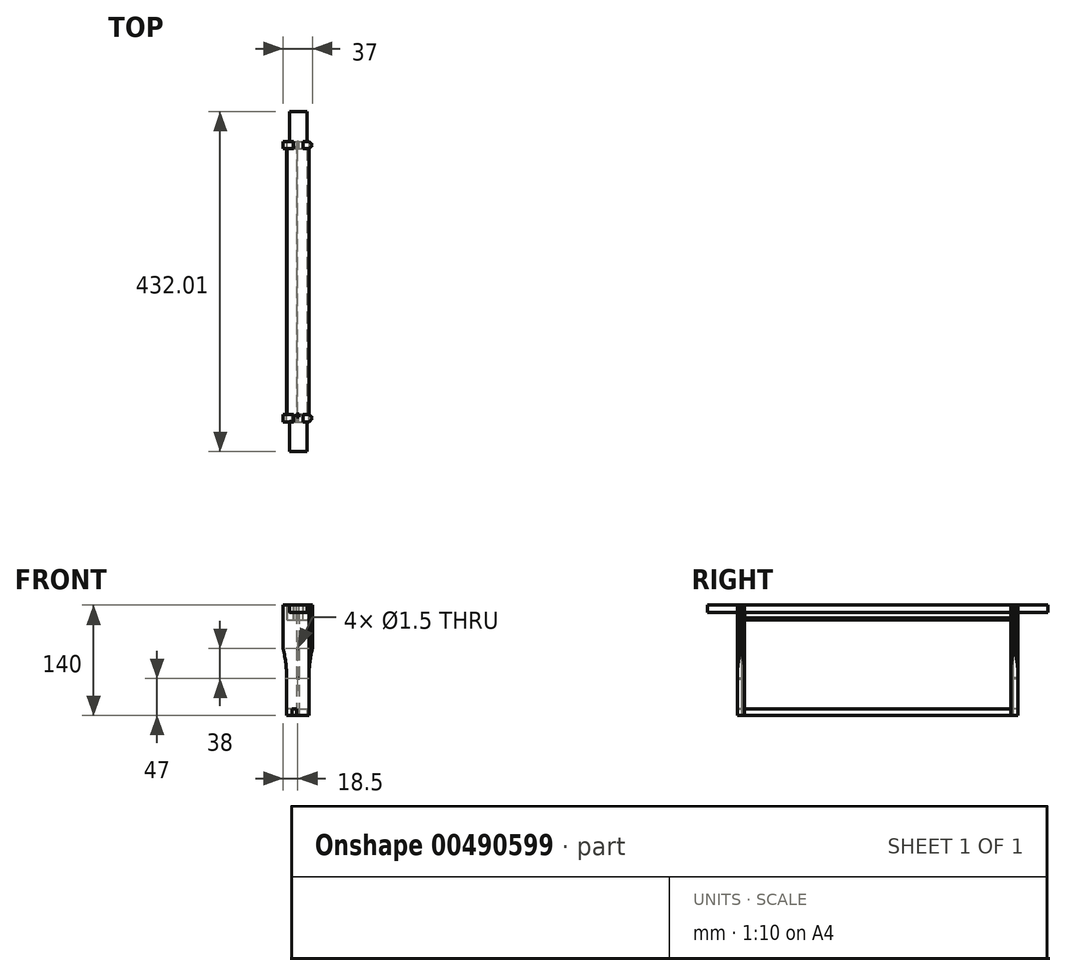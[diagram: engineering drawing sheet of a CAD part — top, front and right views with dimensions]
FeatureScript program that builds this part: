
annotation { "Feature Type Name" : "Feature", "Feature Type Description" : "" }
export const myFeature = defineFeature(function(context is Context, id is Id, definition is map)
    precondition{}
    {
        {
            var Q0;
            Q0=qCreatedBy(makeId("Top.planeOp"),FACE);
            var sketch = newSketch(context, id + "F0", { "sketchPlane" : qUnion([Q0])});
            skLineSegment(sketch, "E0", {"start": v(19.05, -9) * mm, "end": v(19.05, 383.16) * mm, "construction": true});
            skLineSegment(sketch, "E1.0", {"start": v(33.05, 0.03) * mm, "end": v(33.05, 338.03) * mm});
            skLineSegment(sketch, "E2.0", {"start": v(5.05, 0.04) * mm, "end": v(5.05, 338.03) * mm});
            skLineSegment(sketch, "E3.0", {"start": v(5.05, 338.03) * mm, "end": v(13.05, 338.03) * mm});
            skPoint(sketch, "E4.orphan", {"position": v(0.35, 338.03) * mm});
            skLineSegment(sketch, "E5.0", {"start": v(25.05, 338.04) * mm, "end": v(33.05, 338.03) * mm});
            skLineSegment(sketch, "E5.1", {"start": v(25.05, 347.04) * mm, "end": v(25.05, 338.04) * mm});
            skLineSegment(sketch, "E5.2", {"start": v(13.05, 347.03) * mm, "end": v(13.05, 338.03) * mm});
            skLineSegment(sketch, "E5.3", {"start": v(8.05, 347.03) * mm, "end": v(13.05, 347.03) * mm});
            skLineSegment(sketch, "E5.4", {"start": v(25.05, 347.04) * mm, "end": v(30.05, 347.04) * mm});
            skPoint(sketch, "E6.orphan", {"position": v(33.25, 338.03) * mm});
            skPoint(sketch, "E7.orphan", {"position": v(33.23, 347.04) * mm});
            skLineSegment(sketch, "E8", {"start": v(8.05, 347.03) * mm, "end": v(8.05, 385.04) * mm});
            skLineSegment(sketch, "E9", {"start": v(30.05, 347.04) * mm, "end": v(30.05, 385.04) * mm});
            skLineSegment(sketch, "E10", {"start": v(8.05, 385.04) * mm, "end": v(30.05, 385.04) * mm});
            skPoint(sketch, "E11.orphan", {"position": v(0.35, 347.03) * mm});
            skPoint(sketch, "E12.endSnap0", {"position": v(19.05, 187.08) * mm});
            skLineSegment(sketch, "E13.0", {"start": v(25.05, 0.03) * mm, "end": v(33.05, 0.03) * mm});
            skLineSegment(sketch, "E13.1", {"start": v(5.05, 0.04) * mm, "end": v(13.05, 0.04) * mm});
            skPoint(sketch, "E14.orphan", {"position": v(0, 0.04) * mm});
            skPoint(sketch, "E15.orphan", {"position": v(33.6, 0.03) * mm});
            skLineSegment(sketch, "E16", {"start": v(19.05, 169.03) * mm, "end": v(85.88, 169.03) * mm, "construction": true});
            skPoint(sketch, "E16.startSnap0", {"position": v(5.05, 169.03) * mm});
            skPoint(sketch, "E16.endSnap0", {"position": v(33.05, 169.03) * mm});
            skLineSegment(sketch, "E17.MirrorCS", {"start": v(8.05, -8.87) * mm, "end": v(13.05, -8.87) * mm});
            skLineSegment(sketch, "E18.MirrorCS", {"start": v(8.05, -8.87) * mm, "end": v(8.05, -46.97) * mm});
            skLineSegment(sketch, "E19.MirrorCS", {"start": v(8.05, -46.97) * mm, "end": v(30.05, -46.97) * mm});
            skLineSegment(sketch, "E20.MirrorCS", {"start": v(30.05, -8.97) * mm, "end": v(30.05, -46.97) * mm});
            skLineSegment(sketch, "E21.MirrorCS", {"start": v(25.05, -8.97) * mm, "end": v(30.05, -8.97) * mm});
            skLineSegment(sketch, "E22.MirrorCS", {"start": v(25.05, -8.97) * mm, "end": v(25.05, 0.03) * mm});
            skLineSegment(sketch, "E23.MirrorCS", {"start": v(13.05, -8.87) * mm, "end": v(13.05, 0.04) * mm});
            skPoint(sketch, "E24.orphan", {"position": v(30.05, 347.04) * mm});
            skSolve(sketch);
        }
        {
            var Q0;
            Q0=qSketchRegion(id+"F0",true);
            var Q1;
            Q1=makeQuery(id+"F10.opExtrude","SWEPT_FACE",FACE,{"disambiguationData":[OSD([sQuery(id+"F9.wireOp",EDGE,"E41.bottom")])]});
            extrude(context, id + "F1", {"entities" : qUnion([Q0]), "oppositeDirection" : true, "endBoundEntityFace" : qUnion([Q1]), "depth" : 19.05 * mm});
        }
        {
            var Q0;
            Q0=makeQuery(id+"F1.opExtrude","SWEPT_FACE",FACE,{"disambiguationData":[OSD([sQuery(id+"F0.wireOp",EDGE,"E13.0")])]});
            var sketch = newSketch(context, id + "F2", { "sketchPlane" : qUnion([Q0])});
            skPoint(sketch, "E25.startSnap0", {"position": v(19.05, -19.05) * mm});
            skLineSegment(sketch, "E26", {"start": v(37.4, -9.53) * mm, "end": v(17.41, -9.53) * mm});
            skPoint(sketch, "E26.startSnap0", {"position": v(30.05, -9.53) * mm});
            skLineSegment(sketch, "E27", {"start": v(37.4, -24.9) * mm, "end": v(17.41, -24.9) * mm});
            skLineSegment(sketch, "E28", {"start": v(37.4, -9.53) * mm, "end": v(37.4, -24.9) * mm});
            skLineSegment(sketch, "E29", {"start": v(17.41, -24.9) * mm, "end": v(17.41, -9.53) * mm});
            skSolve(sketch);
        }
        {
            var Q0;
            Q0=qSketchRegion(id+"F2",true);
            var Q1;
            Q1=makeQuery(id+"F1.opExtrude","SWEPT_FACE",FACE,{"disambiguationData":[OSD([sQuery(id+"F0.wireOp",EDGE,"E5.0")])]});
            extrude(context, id + "F3", {"entities" : qUnion([Q0]), "operationType" : NewBodyOperationType.REMOVE, "endBound" : BoundingType.UP_TO_SURFACE, "oppositeDirection" : true, "endBoundEntityFace" : qUnion([Q1]), "depth" : 25.4 * mm});
        }
        {
            var Q0;
            Q0=makeQuery(id+"F1.opExtrude","SWEPT_FACE",FACE,{"disambiguationData":[OSD([sQuery(id+"F0.wireOp",EDGE,"E1.0")])]});
            var sketch = newSketch(context, id + "F4", { "sketchPlane" : qUnion([Q0])});
            skLineSegment(sketch, "E30", {"start": v(0, -9.53) * mm, "end": v(0, -22.59) * mm});
            skLineSegment(sketch, "E31", {"start": v(338, -9.53) * mm, "end": v(338, -24.25) * mm});
            skLineSegment(sketch, "E32.0", {"start": v(394.42, -9.53) * mm, "end": v(338.03, -9.53) * mm});
            skPoint(sketch, "E33.orphan", {"position": v(0.03, -9.53) * mm});
            skLineSegment(sketch, "E34", {"start": v(-57.04, -9.53) * mm, "end": v(-57.04, -22.21) * mm});
            skLineSegment(sketch, "E35", {"start": v(-57.04, -22.21) * mm, "end": v(0, -22.59) * mm});
            skPoint(sketch, "E36.orphan", {"position": v(338.03, -9.53) * mm});
            skLineSegment(sketch, "E37", {"start": v(338, -24.25) * mm, "end": v(394.57, -24.25) * mm});
            skLineSegment(sketch, "E38", {"start": v(394.57, -24.25) * mm, "end": v(394.42, -9.53) * mm});
            skLineSegment(sketch, "E39.trimOffspring", {"start": v(0.03, -9.53) * mm, "end": v(-57.04, -9.53) * mm});
            skSolve(sketch);
        }
        {
            var Q0;
            {var subQ0=sQuery(id+"F4.wireOp",EDGE,"E30");Q0=makeQuery(id+"F4.imprint","IMPRINT",FACE,{"disambiguationData":[TD([[makeQuery(id+"F4.imprint","IMPRINT",EDGE,{"derivedFrom":subQ0}),-1.0]])]});}
            var Q1;
            {var subQ1=sQuery(id+"F4.wireOp",EDGE,"E31");Q1=makeQuery(id+"F4.imprint","IMPRINT",FACE,{"disambiguationData":[TD([[makeQuery(id+"F4.imprint","IMPRINT",EDGE,{"derivedFrom":subQ1}),1.0]])]});}
            var Q2;
            Q2=makeQuery(id+"F3.boolean.opBoolean","COPY",FACE,{"derivedFrom":makeQuery(id+"F3.opExtrude","SWEPT_FACE",FACE,{"disambiguationData":[OSD([sQuery(id+"F2.wireOp",EDGE,"E25")])]})});
            extrude(context, id + "F5", {"entities" : qUnion([Q0, Q1]), "operationType" : NewBodyOperationType.REMOVE, "endBound" : BoundingType.THROUGH_ALL, "oppositeDirection" : true, "endBoundEntityFace" : qUnion([Q2]), "depth" : 25.4 * mm});
        }
        {
            var Q0;
            Q0=makeQuery(id+"F1.opExtrude","SWEPT_FACE",FACE,{"disambiguationData":[OSD([sQuery(id+"F0.wireOp",EDGE,"E1.0")])]});
            var sketch = newSketch(context, id + "F6", { "sketchPlane" : qUnion([Q0])});
            skLineSegment(sketch, "E40.0.0", {"start": v(0.03, -19.05) * mm, "end": v(338, -19.05) * mm});
            skLineSegment(sketch, "E40.0.1", {"start": v(338, -19.05) * mm, "end": v(338, -9.53) * mm});
            skLineSegment(sketch, "E40.0.2", {"start": v(338, -9.53) * mm, "end": v(0.03, -9.53) * mm});
            skLineSegment(sketch, "E40.0.3", {"start": v(0.03, -9.53) * mm, "end": v(0.03, -19.05) * mm});
            skSolve(sketch);
        }
        {
            var Q0;
            Q0=qSketchRegion(id+"F6",true);
            extrude(context, id + "F7", {"entities" : qUnion([Q0]), "oppositeDirection" : true, "depth" : 15 * mm});
        }
        {
            var Q0;
            Q0=makeQuery(id+"F7.opExtrude","CAP_EDGE",EDGE,{"disambiguationData":[OSD([sQuery(id+"F6.wireOp",EDGE,"E40.0.0")])],"isStart":true});
            chamfer(context, id + "F8", {"entities" : qUnion([Q0]), "width" : 3 * mm, "tangentPropagation" : true});
        }
        {
            var Q0;
            Q0=qCreatedBy(makeId("Front.planeOp"),FACE);
            var sketch = newSketch(context, id + "F9", { "sketchPlane" : qUnion([Q0])});
            skLineSegment(sketch, "E41.bottom", {"start": v(0, 0) * mm, "end": v(13, 0) * mm});
            skLineSegment(sketch, "E42", {"start": v(13, -9) * mm, "end": v(25, -9) * mm});
            skPoint(sketch, "E43.orphan", {"position": v(18.5, 0) * mm});
            skLineSegment(sketch, "E44.trimOffspring", {"start": v(25, 0) * mm, "end": v(37, 0) * mm});
            skLineSegment(sketch, "E45", {"start": v(18.5, -140) * mm, "end": v(18.5, 131.81) * mm, "construction": true});
            skPoint(sketch, "E45.endSnap0", {"position": v(18.5, -93) * mm});
            skPoint(sketch, "E46.orphan", {"position": v(-1.11, -140) * mm});
            skPoint(sketch, "E47.orphan", {"position": v(38.11, -140) * mm});
            skLineSegment(sketch, "E48.0", {"start": v(11, -132) * mm, "end": v(17, -132) * mm});
            skLineSegment(sketch, "E49.trimOffspring", {"start": v(17, -140) * mm, "end": v(32.5, -140) * mm});
            skCircle(sketch, "E50", {"center": v(18.5, -93) * mm, "radius": 0.75 * mm});
            skLineSegment(sketch, "E51.direction2", {"start": v(18.5, -93) * mm, "end": v(18.5, -131) * mm, "construction": true});
            skCircle(sketch, "E52", {"center": v(18.5, -55) * mm, "radius": 0.75 * mm});
            skLineSegment(sketch, "E53", {"start": v(17, -132) * mm, "end": v(17, -140) * mm});
            skLineSegment(sketch, "E54", {"start": v(32.5, -140) * mm, "end": v(32.5, -95) * mm});
            skLineSegment(sketch, "E55", {"start": v(4.5, -95) * mm, "end": v(4.5, -140) * mm});
            skLineSegment(sketch, "E56", {"start": v(0, -55) * mm, "end": v(0, 0) * mm});
            skLineSegment(sketch, "E57", {"start": v(37, -55) * mm, "end": v(37, 0) * mm});
            skLineSegment(sketch, "E58", {"start": v(25, 0) * mm, "end": v(25, -9) * mm});
            skLineSegment(sketch, "E59", {"start": v(13, 0) * mm, "end": v(13, -9) * mm});
            skArc(sketch, "E60", {"start": v(37, -55) * mm, "mid": v(33.63, -74.87) * mm, "end": v(32.5, -95) * mm});
            skArc(sketch, "E61.MirrorCS", {"start": v(0, -55) * mm, "mid": v(3.37, -74.87) * mm, "end": v(4.5, -95) * mm});
            skPoint(sketch, "E62.end.orphan", {"position": v(32.5, 70.86) * mm});
            skPoint(sketch, "E63.orphan", {"position": v(4.5, 70.86) * mm});
            skLineSegment(sketch, "E64", {"start": v(11, -132) * mm, "end": v(11, -140) * mm});
            skLineSegment(sketch, "E65", {"start": v(11, -140) * mm, "end": v(4.5, -140) * mm});
            skSolve(sketch);
        }
        {
            var Q0;
            Q0=qSketchRegion(id+"F9",true);
            extrude(context, id + "F10", {"entities" : qUnion([Q0]), "depth" : 9 * mm});
        }
        {
            var Q0;
            Q0=qCreatedBy(makeId("Top.planeOp"),FACE);
            var sketch = newSketch(context, id + "F11", { "sketchPlane" : qUnion([Q0])});
            skLineSegment(sketch, "E66.top", {"start": v(17, -3.2) * mm, "end": v(20, -3.2) * mm});
            skLineSegment(sketch, "E66.left", {"start": v(17, 0.82) * mm, "end": v(17, -3.2) * mm});
            skLineSegment(sketch, "E66.right", {"start": v(20, 0.82) * mm, "end": v(20, -3.2) * mm});
            skLineSegment(sketch, "E67", {"start": v(17, 0.82) * mm, "end": v(20, 0.82) * mm});
            skLineSegment(sketch, "E68.0", {"start": v(37, -9) * mm, "end": v(37, 0) * mm});
            skLineSegment(sketch, "E69", {"start": v(37, -4.5) * mm, "end": v(33.08, 0) * mm});
            skLineSegment(sketch, "E70", {"start": v(37, -4.5) * mm, "end": v(32.95, -4.5) * mm, "construction": true});
            skLineSegment(sketch, "E71.MirrorCS", {"start": v(37, -4.5) * mm, "end": v(33.08, -9) * mm});
            skLineSegment(sketch, "E72", {"start": v(33.08, 0) * mm, "end": v(38.38, 3.06) * mm});
            skLineSegment(sketch, "E73", {"start": v(38.38, 3.06) * mm, "end": v(38.38, -11.94) * mm});
            skLineSegment(sketch, "E74", {"start": v(38.38, -11.94) * mm, "end": v(33.08, -9) * mm});
            skSolve(sketch);
        }
        {
            var Q0;
            Q0=qSketchRegion(id+"F11",true);
            extrude(context, id + "F12", {"entities" : qUnion([Q0]), "operationType" : NewBodyOperationType.REMOVE, "endBound" : BoundingType.THROUGH_ALL, "oppositeDirection" : true, "depth" : 25.4 * mm});
        }
        {
            var Q0;
            Q0=qCreatedBy(makeId("Front.planeOp"),FACE);
            cPlane(context, id + "F13", {"entities" : qUnion([Q0]), "cplaneType" : CPlaneType.OFFSET, "offset" : 338 * mm / 2, "oppositeDirection" : true, "width" : 152.4 * mm, "height" : 152.4 * mm});
        }
        {
            var Q0;
            Q0=makeQuery(id+"F10.opExtrude","SWEPT_BODY",BODY,{"disambiguationData":[OSD([sQuery(id+"F9.wireOp",EDGE,"E41.bottom"),sQuery(id+"F9.wireOp",EDGE,"E41.top"),sQuery(id+"F9.wireOp",EDGE,"E41.left"),sQuery(id+"F9.wireOp",EDGE,"E41.right"),sQuery(id+"F9.wireOp",EDGE,"4409148b-b390-4e07-baa5-3b63a4127629.0"),sQuery(id+"F9.wireOp",EDGE,"E42"),sQuery(id+"F9.wireOp",EDGE,"E44.trimOffspring"),sQuery(id+"F9.wireOp",EDGE,"b8636df0-6067-4348-a966-9dc5cb130c67.0"),sQuery(id+"F9.wireOp",EDGE,"62ecbbba-ad5a-4f04-9f53-49cf14ff5d85.0"),sQuery(id+"F9.wireOp",EDGE,"E62"),sQuery(id+"F9.wireOp",EDGE,"5f9efb45-4930-4ef4-83bc-05483749d9d60.MirrorCS"),sQuery(id+"F9.wireOp",EDGE,"8d248a55-4712-4b9c-8aae-286cf1399562.0"),sQuery(id+"F9.wireOp",EDGE,"0ee37a51-297f-4fc0-93e2-258c872eef24.0"),sQuery(id+"F9.wireOp",EDGE,"E48.0"),sQuery(id+"F9.wireOp",EDGE,"1bf6711e-7a88-4e91-bf7f-35fa35dde198.0"),sQuery(id+"F9.wireOp",EDGE,"25d5550f-5548-4780-a67b-c3ee72b3c1fd.0"),sQuery(id+"F9.wireOp",EDGE,"1f51d974-8474-4bfa-9081-1fb003eba0a6.trimOffspring"),sQuery(id+"F9.wireOp",EDGE,"E49.trimOffspring"),sQuery(id+"F9.wireOp",EDGE,"5dedfb5b-1bd9-44c2-91e4-66f6d98deb70.trimOffspring"),sQuery(id+"F9.wireOp",EDGE,"E50"),sQuery(id+"F9.wireOp",EDGE,"E51.0.1.0"),sQuery(id+"F9.wireOp",EDGE,"E51.0.2.0"),sQuery(id+"F9.wireOp",EDGE,"E51.0.3.0"),sQuery(id+"F9.wireOp",EDGE,"E51.0.4.0"),sQuery(id+"F9.wireOp",EDGE,"E52"),sQuery(id+"F9.wireOp",EDGE,"RnglHFMx-U6fH-N23S-GqXE-xkk8O2uPKiBN")])]});
            var Q1;
            Q1=qCreatedBy(id+"F13.planeOp",FACE);
            mirror(context, id + "F14", {"entities" : qUnion([Q0]), "mirrorPlane" : qUnion([Q1])});
        }
        {
            var Q0;
            Q0=makeQuery(id+"F10.opExtrude","SWEPT_FACE",FACE,{"disambiguationData":[OSD([sQuery(id+"F9.wireOp",EDGE,"E49.trimOffspring")])]});
            var sketch = newSketch(context, id + "F15", { "sketchPlane" : qUnion([Q0])});
            skLineSegment(sketch, "E75.0", {"start": v(11, 9) * mm, "end": v(11, 0) * mm});
            skLineSegment(sketch, "E76.0.0", {"start": v(18.05, -338) * mm, "end": v(30.05, -338) * mm});
            skLineSegment(sketch, "E76.0.1", {"start": v(30.05, -338) * mm, "end": v(30.05, -0.03) * mm});
            skLineSegment(sketch, "E76.0.2", {"start": v(30.05, -0.03) * mm, "end": v(18.05, -0.03) * mm});
            skLineSegment(sketch, "E76.0.3", {"start": v(18.05, -0.03) * mm, "end": v(18.05, -338) * mm});
            skLineSegment(sketch, "E77.0", {"start": v(11, 0) * mm, "end": v(4.5, 0) * mm});
            skLineSegment(sketch, "E78.0", {"start": v(11, -338) * mm, "end": v(4.5, -338) * mm});
            skLineSegment(sketch, "E78.1", {"start": v(11, -347) * mm, "end": v(11, -338) * mm});
            skLineSegment(sketch, "E79", {"start": v(4.5, 0) * mm, "end": v(4.5, -338) * mm});
            skLineSegment(sketch, "E80.0", {"start": v(11, -347) * mm, "end": v(17, -347) * mm});
            skLineSegment(sketch, "E81.0", {"start": v(11, 9) * mm, "end": v(11, 9) * mm});
            skLineSegment(sketch, "E82", {"start": v(17, -347) * mm, "end": v(17, 9) * mm});
            skLineSegment(sketch, "E83", {"start": v(17, 9) * mm, "end": v(11, 9) * mm});
            skSolve(sketch);
        }
        {
            var Q0;
            Q0=qSketchRegion(id+"F15",true);
            var Q1;
            Q1=makeQuery(id+"F10.opExtrude","SWEPT_FACE",FACE,{"disambiguationData":[OSD([sQuery(id+"F9.wireOp",EDGE,"E48.0")])]});
            extrude(context, id + "F16", {"entities" : qUnion([Q0]), "endBound" : BoundingType.UP_TO_SURFACE, "oppositeDirection" : true, "endBoundEntityFace" : qUnion([Q1]), "depth" : 25 * mm});
        }
    });
